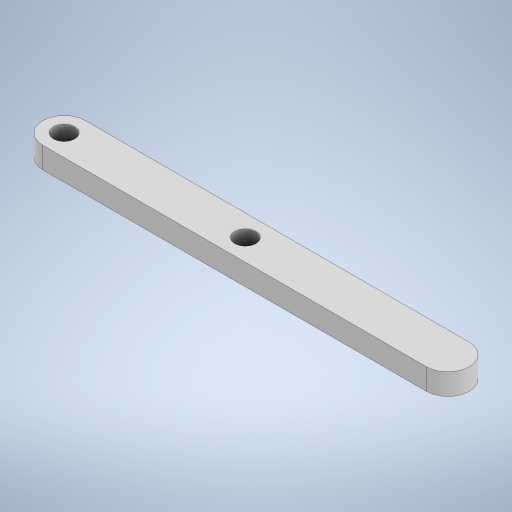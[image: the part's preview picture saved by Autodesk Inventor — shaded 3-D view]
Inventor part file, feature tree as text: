
AUTODESK INVENTOR PART (.ipt)
format: ipt  version: 2024 (Build 280153000, 153)  size: 241,152 bytes
history: native  units: mm
features: sketch x3, hole x2, extrude x1
ambient origin geometry x8: Origin, YZ Plane, XZ Plane, XY Plane, X Axis, Y Axis, Z Axis, Center Point
bodies: Volumenkörper1 (feature_tree)
feature tree (6):
  extrude  "Extrusion1"  Depth=10.0mm
  hole  "Bohrung1"  [1 undecoded]
  hole  "Bohrung2"  [1 undecoded]
  sketch  "Skizze1"  dims[d0=90.0mm d1=10.0mm]
  sketch  "Skizze2"  dims[d2=5.0mm d3=0.0mm]
  sketch  "Skizze3"  dims[d4=5.0mm d5=6.0mm d6=8.0mm d7=4.6mm d8=90.0deg d9=8.0mm d10=20.594885mm d11=42.5mm d12=5.0mm d13=6.0mm d14=4.0mm d15=2.0mm d16=90.0deg d17=8.0mm d18=20.594885mm]
note: 2 required parameter values undecoded (feature->parameter linkage not recoverable at this tier; creation-order binding heuristic only, values carry confidence <= 0.55)
